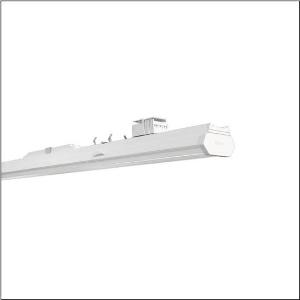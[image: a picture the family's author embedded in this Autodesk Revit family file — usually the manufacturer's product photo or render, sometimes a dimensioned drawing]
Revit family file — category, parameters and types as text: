
# Revit family: licross_r__21_protected_ho_52td11dn4e5s_21e0
name_source: partatom
category: Lighting Fixtures
units: mm (PartAtom-declared; Revit-internal decimal feet)

## family parameters
Cut with Voids When Loaded = No
Host = Face
Light Source = No
Part Type = Normal
Room Calculation Point = No
Round Connector Dimension = Use Diameter
Shared = No

## types (1)
- --- (1 x LED, 14920 lm, 84.9 W, 4000K)
    Apparent Load = 85 VA
    CIE Flux Codes = 84 94 98 99 100
    Color Rendering = 80
    Color Temperature = 4000K
    Default Elevation = 1800 mm
    Description = Licross® 21 Protected HO, luminaire insert, of sheet steel, galvanised, coil coated, white, length: 1.500mm, width: 90mm, height: 103mm, LED rated luminous flux: 14.920lm, light colour: 840, control gear: DALI 2, with plug, 5-pole, with phase selection, mains connection: 220..240V, AC, 50/60Hz, rated input power: 85W, halogen-free wiring, primary light control with lens, of plastic, primary optical cover: cover, of PMMA, light emission: direct distribution, primary light characteristic: symmetric, protection rating (complete): IP54, insulation class (complete): insulation class I (protective earthing), certification: CE, ENEC, VDE, UKCA, protection symbol: D if used in an environment with non-conductive dust loads with corresponding accessories, impact resistance: IK06, permissible ambient temperature for indoor applications: -25..+35°C, corresponds to IFS (International Featured Standards) requirements for safety and quality in the food industry, reducing of maximum allowable ambient temperature of 5°C with ceiling mounting, LABS conformity tested according to VDMA 24364:2018-05, packaging unit: 1 piece
    Height = 92 mm
    Lamp = 1 x LED
    Lamp Light Flux = 14920 lm
    Lamp Power = 84.9 W
    Lamp count = 1
    Length = 1500 mm
    Luminous efficacy = 176 lm/W
    Manufacturer = Siteco
    ModVariant = No
    Model = 52TD11DN4E5S
    Mounting Place = Ceiling
    Mounting Type = Pendant
    Number of Poles = 1
    OnlyDefault = Yes
    Power Factor = 1
    Product Name = Licross® 21 Protected HO
    Product group = luminaire insert
    ProductGroupID = 901
    Protection Class = Protection class I
    Protection Degree = IP 54
    RLX_Detail_Level = 1
    RLX_Emergency_Light_Flux = 0 lm
    RLX_Emergency_Type = 0
    RLX_Emergency_Type_DB = No
    RlxData = <blob elided: 24369 chars, md5=fdd1bd40>
    Socket = socket
    Standby Power = 0 W
    System Light Flux = 14920 lm
    System Power = 85 W
    Type Comments = factory setting: luminous flux: 100 % | dim-lin: 254 | 484 mA
    Type Image = l_1256148.jpg
    URL = http://relux.com
    VarID = @adj_078241
    Voltage = 0 V
    Weight = 0.00 kg
    Width = 88 mm

## geometry (parser evidence)
native form markers: Blend x4, Sweep x9
no freeform markers — native parametric forms only
